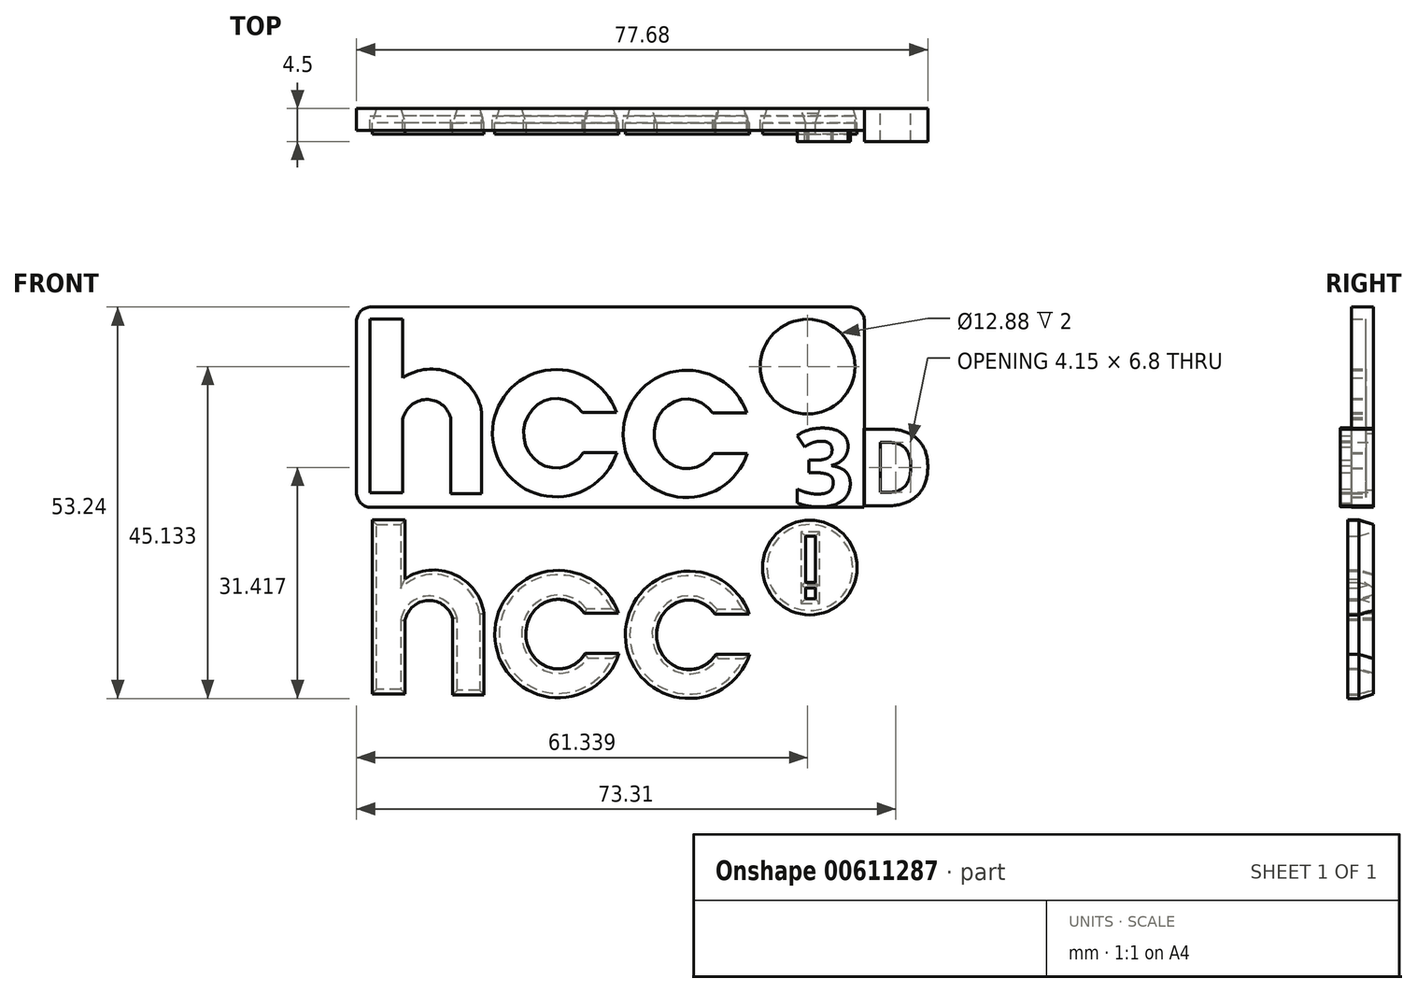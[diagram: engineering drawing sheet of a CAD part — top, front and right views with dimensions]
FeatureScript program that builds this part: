
annotation { "Feature Type Name" : "Feature", "Feature Type Description" : "" }
export const myFeature = defineFeature(function(context is Context, id is Id, definition is map)
    precondition{}
    {
        {
            var Q0;
            Q0=qCreatedBy(makeId("Front.planeOp"),FACE);
            var sketch = newSketch(context, id + "F0", { "sketchPlane" : qUnion([Q0])});
            skLineSegment(sketch, "E0.bottom", {"start": v(32.84, -11.61) * mm, "end": v(-34.55, -11.61) * mm});
            skLineSegment(sketch, "E0.top", {"start": v(32.84, 13.5) * mm, "end": v(-34.55, 13.5) * mm});
            skLineSegment(sketch, "E0.left", {"start": v(32.84, -11.61) * mm, "end": v(32.84, 13.5) * mm});
            skLineSegment(sketch, "E0.right", {"start": v(-34.55, -11.61) * mm, "end": v(-34.55, 13.5) * mm});
            skLineSegment(sketch, "E1.bottom", {"start": v(32.84, -2.93) * mm, "end": v(35.45, -2.93) * mm});
            skLineSegment(sketch, "E1.top", {"start": v(32.84, -10.58) * mm, "end": v(35.45, -10.58) * mm});
            skLineSegment(sketch, "E1.left", {"start": v(32.84, -2.93) * mm, "end": v(32.84, -10.58) * mm});
            skLineSegment(sketch, "E1.right", {"start": v(35.45, -2.93) * mm, "end": v(35.45, -10.58) * mm});
            skSolve(sketch);
        }
        {
            var Q0;
            Q0=qCreatedBy(makeId("Front.planeOp"),FACE);
            var sketch = newSketch(context, id + "F1", { "sketchPlane" : qUnion([Q0])});
            skLineSegment(sketch, "E2.bottom", {"start": v(-29.23, 12.7) * mm, "end": v(-33.71, 12.7) * mm});
            skLineSegment(sketch, "E2.top", {"start": v(-29.23, -10.95) * mm, "end": v(-33.71, -10.95) * mm});
            skLineSegment(sketch, "E2.left", {"start": v(-29.23, 12.7) * mm, "end": v(-29.23, 4.68) * mm});
            skLineSegment(sketch, "E2.right", {"start": v(-33.71, 12.7) * mm, "end": v(-33.71, -10.95) * mm});
            skArc(sketch, "E3", {"start": v(-18.5, 0) * mm, "mid": v(-22.56, 5.32) * mm, "end": v(-29.23, 4.68) * mm});
            skArc(sketch, "E4", {"start": v(-22.75, -0.72) * mm, "mid": v(-26.08, 1.76) * mm, "end": v(-29.23, -0.94) * mm});
            skLineSegment(sketch, "E5", {"start": v(-22.75, -0.72) * mm, "end": v(-22.75, -11.06) * mm});
            skLineSegment(sketch, "E6", {"start": v(-22.75, -11.06) * mm, "end": v(-18.5, -11.06) * mm});
            skLineSegment(sketch, "E7", {"start": v(-18.5, -11.06) * mm, "end": v(-18.5, 0) * mm});
            skArc(sketch, "E8", {"start": v(-0.2, 0) * mm, "mid": v(-17.04, -2.91) * mm, "end": v(-0.14, -5.47) * mm});
            skEllipticalArc(sketch, "E9", {});
            skLineSegment(sketch, "E10", {"start": v(-4.83, 0) * mm, "end": v(0, 0) * mm});
            skLineSegment(sketch, "E11", {"start": v(-4.72, -5.47) * mm, "end": v(0, -5.47) * mm});
            skArc(sketch, "E12", {"start": v(17.56, -0.1) * mm, "mid": v(0.73, -3) * mm, "end": v(17.62, -5.56) * mm});
            skEllipticalArc(sketch, "E13", {});
            skLineSegment(sketch, "E14", {"start": v(12.93, -0.1) * mm, "end": v(17.76, -0.1) * mm});
            skLineSegment(sketch, "E15", {"start": v(13.05, -5.56) * mm, "end": v(17.76, -5.56) * mm});
            skCircle(sketch, "E16", {"center": v(25.8, 6.23) * mm, "radius": 6.44 * mm});
            skLineSegment(sketch, "E17.bottom", {"start": v(25.21, 10.49) * mm, "end": v(26.54, 10.49) * mm});
            skLineSegment(sketch, "E17.top", {"start": v(25.21, 4.24) * mm, "end": v(26.54, 4.24) * mm});
            skLineSegment(sketch, "E17.left", {"start": v(25.21, 10.49) * mm, "end": v(25.21, 4.24) * mm});
            skLineSegment(sketch, "E17.right", {"start": v(26.54, 10.49) * mm, "end": v(26.54, 4.24) * mm});
            skLineSegment(sketch, "E18.bottom", {"start": v(25.21, 3.44) * mm, "end": v(26.54, 3.44) * mm});
            skLineSegment(sketch, "E18.top", {"start": v(25.21, 1.98) * mm, "end": v(26.54, 1.98) * mm});
            skLineSegment(sketch, "E18.left", {"start": v(25.21, 3.44) * mm, "end": v(25.21, 1.98) * mm});
            skLineSegment(sketch, "E18.right", {"start": v(26.54, 3.44) * mm, "end": v(26.54, 1.98) * mm});
            skLineSegment(sketch, "E19.bottom", {"start": v(-35.53, 14.34) * mm, "end": v(33.55, 14.34) * mm});
            skLineSegment(sketch, "E19.top", {"start": v(-35.53, -12.91) * mm, "end": v(33.55, -12.91) * mm});
            skLineSegment(sketch, "E19.left", {"start": v(-35.53, 14.34) * mm, "end": v(-35.53, -12.91) * mm});
            skLineSegment(sketch, "E19.right", {"start": v(33.55, 14.34) * mm, "end": v(33.55, -12.91) * mm});
            skPoint(sketch, "E20.orphan", {"position": v(-32.13, 0) * mm});
            skLineSegment(sketch, "E21.trimOffspring", {"start": v(-29.23, -0.94) * mm, "end": v(-29.23, -10.95) * mm});
            skText(sketch, "E22", { "text": "3D", "fontName": "OpenSans-Bold.ttf"});
            skLineSegment(sketch, "E23.bottom", {"start": v(33.46, -2.18) * mm, "end": v(33.55, -2.18) * mm});
            skLineSegment(sketch, "E23.top", {"start": v(33.46, -2.18) * mm, "end": v(33.55, -2.18) * mm});
            skLineSegment(sketch, "E23.left", {"start": v(33.55, -2.18) * mm, "end": v(33.55, -2.18) * mm});
            skLineSegment(sketch, "E23.right", {"start": v(33.46, -2.18) * mm, "end": v(33.46, -2.18) * mm});
            skLineSegment(sketch, "E24.bottom", {"start": v(33.55, -12.71) * mm, "end": v(33.46, -12.71) * mm});
            skLineSegment(sketch, "E24.top", {"start": v(33.55, -12.91) * mm, "end": v(33.46, -12.91) * mm});
            skLineSegment(sketch, "E24.left", {"start": v(33.46, -12.91) * mm, "end": v(33.46, -12.71) * mm});
            skLineSegment(sketch, "E24.right", {"start": v(33.55, -12.91) * mm, "end": v(33.55, -12.71) * mm});
            skLineSegment(sketch, "E25.bottom", {"start": v(33.64, -12.71) * mm, "end": v(33.46, -12.71) * mm});
            skLineSegment(sketch, "E25.top", {"start": v(33.55, -2.18) * mm, "end": v(33.46, -2.18) * mm});
            skLineSegment(sketch, "E25.left", {"start": v(33.46, -12.71) * mm, "end": v(33.46, -2.18) * mm});
            skLineSegment(sketch, "E26.top", {"start": v(33.46, -2.76) * mm, "end": v(33.55, -2.76) * mm});
            skLineSegment(sketch, "E26.left", {"start": v(33.55, -2.18) * mm, "end": v(33.55, -2.76) * mm});
            skLineSegment(sketch, "E26.right", {"start": v(33.46, -2.18) * mm, "end": v(33.46, -2.76) * mm});
            skLineSegment(sketch, "E27.left", {"start": v(33.55, -3.88) * mm, "end": v(33.55, -12.94) * mm});
            skPoint(sketch, "E28.end.orphan", {"position": v(36.71, 0) * mm});
            skPoint(sketch, "E28.start.orphan", {"position": v(33.55, 0) * mm});
            const initialGuessF1  = {"E9": [-0.00838379468768835, -0.002821371890604496, 0, 1, 0.004734611138701439, 0.0044216665190650265, 5.350779379737523, 4.11952951118792], "E13": [0.009380069561302662, -0.0029154655057936907, 0, 1, 0.004734611138701439, 0.0044216665190650265, 5.350779379737523, 4.11952951118792], "E22": [0.02383, -0.01271, 1, 0, 0.01053]};
            skSetInitialGuess(sketch, initialGuessF1);
            skSolve(sketch);
        }
        {
            var Q0;
            Q0 = qSketchRegion(id + "F0", true);
            extrude(context, id + "F2", {"entities" : qUnion([Q0]), "depth" : 1 * mm, "offsetDistance" : 25 * mm});
        }
        {
            var Q0;
            Q0=qCreatedBy(makeId("Front.planeOp"),FACE);
            var sketch = newSketch(context, id + "F3", { "sketchPlane" : qUnion([Q0])});
            skLineSegment(sketch, "E29.bottom", {"start": v(-28.92, -14.64) * mm, "end": v(-33.4, -14.64) * mm});
            skLineSegment(sketch, "E29.top", {"start": v(-28.92, -38.27) * mm, "end": v(-33.4, -38.27) * mm});
            skLineSegment(sketch, "E29.left", {"start": v(-28.92, -14.64) * mm, "end": v(-28.92, -22.65) * mm});
            skLineSegment(sketch, "E29.right", {"start": v(-33.4, -14.64) * mm, "end": v(-33.4, -38.27) * mm});
            skArc(sketch, "E30", {"start": v(-18.2, -27.33) * mm, "mid": v(-22.26, -22) * mm, "end": v(-28.92, -22.65) * mm});
            skArc(sketch, "E31", {"start": v(-22.44, -28.05) * mm, "mid": v(-25.77, -25.57) * mm, "end": v(-28.92, -28.27) * mm});
            skLineSegment(sketch, "E32", {"start": v(-22.44, -28.05) * mm, "end": v(-22.44, -38.39) * mm});
            skLineSegment(sketch, "E33", {"start": v(-22.44, -38.39) * mm, "end": v(-18.2, -38.39) * mm});
            skLineSegment(sketch, "E34", {"start": v(-18.2, -38.39) * mm, "end": v(-18.2, -27.33) * mm});
            skArc(sketch, "E35", {"start": v(0.1, -27.33) * mm, "mid": v(-16.73, -30.24) * mm, "end": v(0.16, -32.8) * mm});
            skEllipticalArc(sketch, "E36", {});
            skLineSegment(sketch, "E37", {"start": v(-4.53, -27.33) * mm, "end": v(0.3, -27.33) * mm});
            skLineSegment(sketch, "E38", {"start": v(-4.41, -32.8) * mm, "end": v(0.3, -32.8) * mm});
            skArc(sketch, "E39", {"start": v(17.87, -27.42) * mm, "mid": v(1.03, -30.33) * mm, "end": v(17.93, -32.89) * mm});
            skEllipticalArc(sketch, "E40", {});
            skLineSegment(sketch, "E41", {"start": v(13.24, -27.42) * mm, "end": v(18.07, -27.42) * mm});
            skLineSegment(sketch, "E42", {"start": v(13.35, -32.89) * mm, "end": v(18.07, -32.89) * mm});
            skCircle(sketch, "E43", {"center": v(26.11, -21.1) * mm, "radius": 6.44 * mm});
            skLineSegment(sketch, "E44.bottom", {"start": v(25.52, -16.84) * mm, "end": v(26.84, -16.84) * mm});
            skLineSegment(sketch, "E44.top", {"start": v(25.52, -23.09) * mm, "end": v(26.84, -23.09) * mm});
            skLineSegment(sketch, "E44.left", {"start": v(25.52, -16.84) * mm, "end": v(25.52, -23.09) * mm});
            skLineSegment(sketch, "E44.right", {"start": v(26.84, -16.84) * mm, "end": v(26.84, -23.09) * mm});
            skLineSegment(sketch, "E45.bottom", {"start": v(25.52, -23.88) * mm, "end": v(26.84, -23.88) * mm});
            skLineSegment(sketch, "E45.top", {"start": v(25.52, -25.35) * mm, "end": v(26.84, -25.35) * mm});
            skLineSegment(sketch, "E45.left", {"start": v(25.52, -23.88) * mm, "end": v(25.52, -25.35) * mm});
            skLineSegment(sketch, "E45.right", {"start": v(26.84, -23.88) * mm, "end": v(26.84, -25.35) * mm});
            skPoint(sketch, "E46.orphan", {"position": v(-31.83, -27.33) * mm});
            skLineSegment(sketch, "E47.trimOffspring", {"start": v(-28.92, -28.27) * mm, "end": v(-28.92, -38.27) * mm});
            const initialGuessF3  = {"E36": [-0.008079084567725658, -0.030148023739457127, 0, 1, 0.004734611138701439, 0.0044216665190650265, 5.350779379737523, 4.11952951118792], "E40": [0.009684779681265354, -0.03024211735464632, 0, 1, 0.004734611138701439, 0.0044216665190650265, 5.350779379737523, 4.11952951118792]};
            skSetInitialGuess(sketch, initialGuessF3);
            skSolve(sketch);
        }
        {
            var Q0;
            Q0=makeQuery(id+"F3.imprint","IMPRINT",FACE,{"disambiguationData":[TD([[makeQuery(id+"F3.imprint","IMPRINT",EDGE,{"derivedFrom":sQuery(id+"F3.wireOp",EDGE,"E29.bottom")}),1.0]])]});
            var Q1;
            {var subQ0=sQuery(id+"F3.wireOp",EDGE,"E35");Q1=makeQuery(id+"F3.imprint","IMPRINT",FACE,{"disambiguationData":[TD([[makeQuery(id+"F3.imprint","IMPRINT",EDGE,{"derivedFrom":subQ0}),1.0]])]});}
            var Q2;
            {var subQ0=sQuery(id+"F3.wireOp",EDGE,"E39");Q2=makeQuery(id+"F3.imprint","IMPRINT",FACE,{"disambiguationData":[TD([[makeQuery(id+"F3.imprint","IMPRINT",EDGE,{"derivedFrom":subQ0}),1.0]])]});}
            var Q3;
            Q3=makeQuery(id+"F3.imprint","IMPRINT",FACE,{"disambiguationData":[TD([[makeQuery(id+"F3.imprint","IMPRINT",EDGE,{"derivedFrom":sQuery(id+"F3.wireOp",EDGE,"E43")}),1.0]])]});
            extrude(context, id + "F4", {"entities" : qUnion([Q0, Q1, Q2, Q3]), "depth" : 3.5 * mm, "offsetDistance" : 25 * mm});
        }
        {
            var Q0;
            Q0=makeQuery(id+"F4.opExtrude","CAP_FACE",FACE,{"disambiguationData":[OSD([sQuery(id+"F3.wireOp",EDGE,"E39"),sQuery(id+"F3.wireOp",EDGE,"E40"),sQuery(id+"F3.wireOp",EDGE,"E41"),sQuery(id+"F3.wireOp",EDGE,"E42")])],"isStart":true});
            var Q1;
            Q1=makeQuery(id+"F4.opExtrude","CAP_EDGE",EDGE,{"disambiguationData":[OSD([sQuery(id+"F3.wireOp",EDGE,"E35")])],"isStart":true});
            var Q2;
            Q2=makeQuery(id+"F4.opExtrude","CAP_EDGE",EDGE,{"disambiguationData":[OSD([sQuery(id+"F3.wireOp",EDGE,"E43")])],"isStart":true});
            var Q3;
            Q3=makeQuery(id+"F4.opExtrude","CAP_EDGE",EDGE,{"disambiguationData":[OSD([sQuery(id+"F3.wireOp",EDGE,"E44.left")])],"isStart":true});
            var Q4;
            Q4=makeQuery(id+"F4.opExtrude","CAP_EDGE",EDGE,{"disambiguationData":[OSD([sQuery(id+"F3.wireOp",EDGE,"E44.bottom")])],"isStart":true});
            var Q5;
            Q5=makeQuery(id+"F4.opExtrude","CAP_EDGE",EDGE,{"disambiguationData":[OSD([sQuery(id+"F3.wireOp",EDGE,"E44.right")])],"isStart":true});
            var Q6;
            Q6=makeQuery(id+"F4.opExtrude","CAP_EDGE",EDGE,{"disambiguationData":[OSD([sQuery(id+"F3.wireOp",EDGE,"E44.top")])],"isStart":true});
            var Q7;
            Q7=makeQuery(id+"F4.opExtrude","CAP_EDGE",EDGE,{"disambiguationData":[OSD([sQuery(id+"F3.wireOp",EDGE,"E45.bottom")])],"isStart":true});
            var Q8;
            Q8=makeQuery(id+"F4.opExtrude","CAP_EDGE",EDGE,{"disambiguationData":[OSD([sQuery(id+"F3.wireOp",EDGE,"E45.left")])],"isStart":true});
            var Q9;
            Q9=makeQuery(id+"F4.opExtrude","CAP_EDGE",EDGE,{"disambiguationData":[OSD([sQuery(id+"F3.wireOp",EDGE,"E45.top")])],"isStart":true});
            var Q10;
            Q10=makeQuery(id+"F4.opExtrude","CAP_EDGE",EDGE,{"disambiguationData":[OSD([sQuery(id+"F3.wireOp",EDGE,"E45.right")])],"isStart":true});
            var Q11;
            Q11=makeQuery(id+"F4.opExtrude","CAP_EDGE",EDGE,{"disambiguationData":[OSD([sQuery(id+"F3.wireOp",EDGE,"E34")])],"isStart":true});
            var Q12;
            Q12=makeQuery(id+"F4.opExtrude","CAP_EDGE",EDGE,{"disambiguationData":[OSD([sQuery(id+"F3.wireOp",EDGE,"E30")])],"isStart":true});
            var Q13;
            Q13=makeQuery(id+"F4.opExtrude","CAP_EDGE",EDGE,{"disambiguationData":[OSD([sQuery(id+"F3.wireOp",EDGE,"E29.left")])],"isStart":true});
            var Q14;
            Q14=makeQuery(id+"F4.opExtrude","CAP_EDGE",EDGE,{"disambiguationData":[OSD([sQuery(id+"F3.wireOp",EDGE,"E29.bottom")])],"isStart":true});
            var Q15;
            Q15=makeQuery(id+"F4.opExtrude","CAP_EDGE",EDGE,{"disambiguationData":[OSD([sQuery(id+"F3.wireOp",EDGE,"E29.right")])],"isStart":true});
            var Q16;
            Q16=makeQuery(id+"F4.opExtrude","CAP_EDGE",EDGE,{"disambiguationData":[OSD([sQuery(id+"F3.wireOp",EDGE,"E29.top")])],"isStart":true});
            var Q17;
            Q17=makeQuery(id+"F4.opExtrude","CAP_EDGE",EDGE,{"disambiguationData":[OSD([sQuery(id+"F3.wireOp",EDGE,"E47.trimOffspring")])],"isStart":true});
            var Q18;
            Q18=makeQuery(id+"F4.opExtrude","CAP_EDGE",EDGE,{"disambiguationData":[OSD([sQuery(id+"F3.wireOp",EDGE,"E31")])],"isStart":true});
            var Q19;
            Q19=makeQuery(id+"F4.opExtrude","CAP_EDGE",EDGE,{"disambiguationData":[OSD([sQuery(id+"F3.wireOp",EDGE,"E32")])],"isStart":true});
            var Q20;
            Q20=makeQuery(id+"F4.opExtrude","CAP_EDGE",EDGE,{"disambiguationData":[OSD([sQuery(id+"F3.wireOp",EDGE,"E33")])],"isStart":true});
            var Q21;
            Q21=makeQuery(id+"F4.opExtrude","CAP_EDGE",EDGE,{"disambiguationData":[OSD([sQuery(id+"F3.wireOp",EDGE,"E36")])],"isStart":true});
            var Q22;
            Q22=makeQuery(id+"F4.opExtrude","CAP_EDGE",EDGE,{"disambiguationData":[OSD([sQuery(id+"F3.wireOp",EDGE,"E38")])],"isStart":true});
            var Q23;
            Q23=makeQuery(id+"F4.opExtrude","CAP_EDGE",EDGE,{"disambiguationData":[OSD([sQuery(id+"F3.wireOp",EDGE,"E37")])],"isStart":true});
            chamfer(context, id + "F5", {"entities" : qUnion([Q0, Q1, Q2, Q3, Q4, Q5, Q6, Q7, Q8, Q9, Q10, Q11, Q12, Q13, Q14, Q15, Q16, Q17, Q18, Q19, Q20, Q21, Q22, Q23]), "chamferType" : ChamferType.TWO_OFFSETS, "width1" : 2 * mm, "oppositeDirection" : false, "width2" : 0.6 * mm, "tangentPropagation" : true});
        }
        {
            var Q0;
            Q0=makeQuery(id+"F1.imprint","IMPRINT",FACE,{"disambiguationData":[TD([[makeQuery(id+"F1.imprint","IMPRINT",EDGE,{"derivedFrom":sQuery(id+"F1.wireOp",EDGE,"E22.sketch_text.stroke-27")}),-1.0]])]});
            var Q1;
            Q1=makeQuery(id+"F1.imprint","IMPRINT",FACE,{"disambiguationData":[TD([[makeQuery(id+"F1.imprint","IMPRINT",EDGE,{"derivedFrom":sQuery(id+"F1.wireOp",EDGE,"E22.sketch_text.stroke-0")}),-1.0]])]});
            extrude(context, id + "F6", {"entities" : qUnion([Q0, Q1]), "operationType" : NewBodyOperationType.ADD, "depth" : 4.5 * mm, "offsetDistance" : 25 * mm});
        }
        {
            var Q0;
            Q0=makeQuery(id+"F1.imprint","IMPRINT",FACE,{"disambiguationData":[TD([[makeQuery(id+"F1.imprint","IMPRINT",EDGE,{"derivedFrom":sQuery(id+"F1.wireOp",EDGE,"E22.sketch_text.stroke-27")}),-1.0]])]});
            var Q1;
            Q1=makeQuery(id+"F1.imprint","IMPRINT",FACE,{"disambiguationData":[TD([[makeQuery(id+"F1.imprint","IMPRINT",EDGE,{"derivedFrom":sQuery(id+"F1.wireOp",EDGE,"E2.bottom")}),-1.0]])]});
            extrude(context, id + "F7", {"entities" : qUnion([Q0, Q1]), "operationType" : NewBodyOperationType.ADD, "depth" : 3 * mm, "offsetDistance" : 25 * mm});
        }
        {
            var Q0;
            Q0=makeQuery(id+"F7.opExtrude","SWEPT_EDGE",EDGE,{"disambiguationData":[OSD([sQuery(id+"F1.wireOp",EDGE,"E19.bottom"),sQuery(id+"F1.wireOp",EDGE,"E19.left")])]});
            var Q1;
            Q1=makeQuery(id+"F7.opExtrude","SWEPT_EDGE",EDGE,{"disambiguationData":[OSD([sQuery(id+"F1.wireOp",EDGE,"E19.top"),sQuery(id+"F1.wireOp",EDGE,"E19.left")])]});
            var Q2;
            Q2=makeQuery(id+"F7.opExtrude","SWEPT_EDGE",EDGE,{"disambiguationData":[OSD([sQuery(id+"F1.wireOp",EDGE,"E19.bottom"),sQuery(id+"F1.wireOp",EDGE,"E19.right")])]});
            fillet(context, id + "F8", {"entities" : qUnion([Q0, Q1, Q2]), "radius" : 2 * mm, "tangentPropagation" : true, "allowEdgeOverflow" : false});
        }
    });
